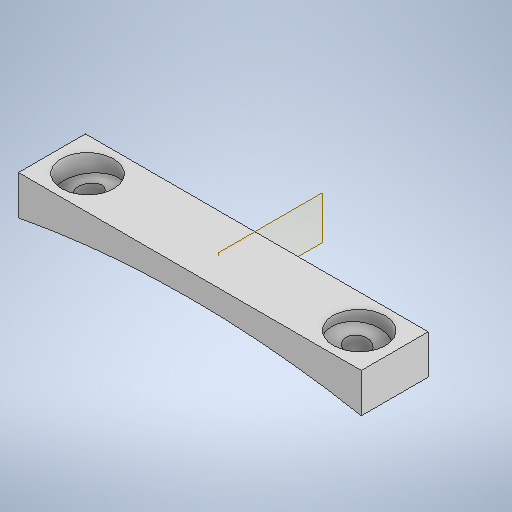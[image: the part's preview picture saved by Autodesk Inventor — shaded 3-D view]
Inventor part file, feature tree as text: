
AUTODESK INVENTOR PART (.ipt)
format: ipt  version: 2025 (Build 290162000, 162)  size: 335,872 bytes
history: native  units: in
note: dims shown in document units (in); Inventor stores cm internally (conversion verified against a paired STEP export)
features: sketch x5, extrude x4, mirror x2, revolve x1, plane x1
ambient origin geometry x8: Origin, YZ Plane, XZ Plane, XY Plane, X Axis, Y Axis, Z Axis, Center Point
bodies: Solid1 (feature_tree)
feature tree (13):
  extrude  "Extrusion1"  Depth=1.5in
  revolve  "Revolution1"  [1 undecoded]
  extrude  "Extrusion2"  Depth=0.0563in
  plane  "Work Plane9"
  mirror  "Mirror1"
  extrude  "Extrusion3"  TaperAngle=90.0deg  [1 undecoded]
  mirror  "Mirror2"
  extrude  "Extrusion4"  TaperAngle=90.0deg  [1 undecoded]
  sketch  "Sketch1"  dims[d2=0.25in d3=1.5in]
  sketch  "Sketch2"  dims[d4=1.0in d5=0.0in d6=0.1in]
  sketch  "Sketch3"  dims[d7=0.12in d8=0.0563in]
  sketch  "Sketch5"  dims[d9=0.2in d10=90.0deg]
  sketch  "Sketch6"  dims[d11=0.275in d12=90.0deg d13=0.15in d14=0.6748in d15=0.1in d16=180.0deg d17=1.0in d18=0.0in d27=-1.8228in d28=1.0in d29=0.0in d30=0.356in d31=90.0deg d32=0.712in d33=1.0in d34=0.0in]
note: 3 required parameter values undecoded (feature->parameter linkage not recoverable at this tier; creation-order binding heuristic only, values carry confidence <= 0.55)